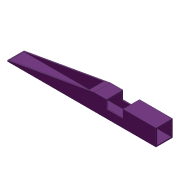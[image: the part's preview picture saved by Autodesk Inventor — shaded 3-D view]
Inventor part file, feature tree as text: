
AUTODESK INVENTOR PART (.ipt)
format: ipt  version: 2012 (Build 160160000, 160)  size: 96,256 bytes
history: native  units: in
note: dims shown in document units (in); Inventor stores cm internally (conversion verified against a paired STEP export)
features: extrude x2, sketch x2, shell x1
ambient origin geometry x8: Origin, YZ Plane, XZ Plane, XY Plane, X Axis, Y Axis, Z Axis, Center Point
bodies: Solid1 (feature_tree)
feature tree (5):
  extrude  "Extrusion1"  Depth=9.0in
  shell  "Shell1"  Thickness=0.0625in
  extrude  "Extrusion2"  Depth=1.0in TaperAngle=0.0deg
  sketch  "Sketch1"  dims[d0=1.0in d1=9.0in d2=0.0625in]
  sketch  "Sketch2"  dims[d3=3.75in d4=1.0in d5=0.0in d6=0.0625in d7=1.0in d8=0.5in d9=2.0in d10=1.0in d11=0.0in]
